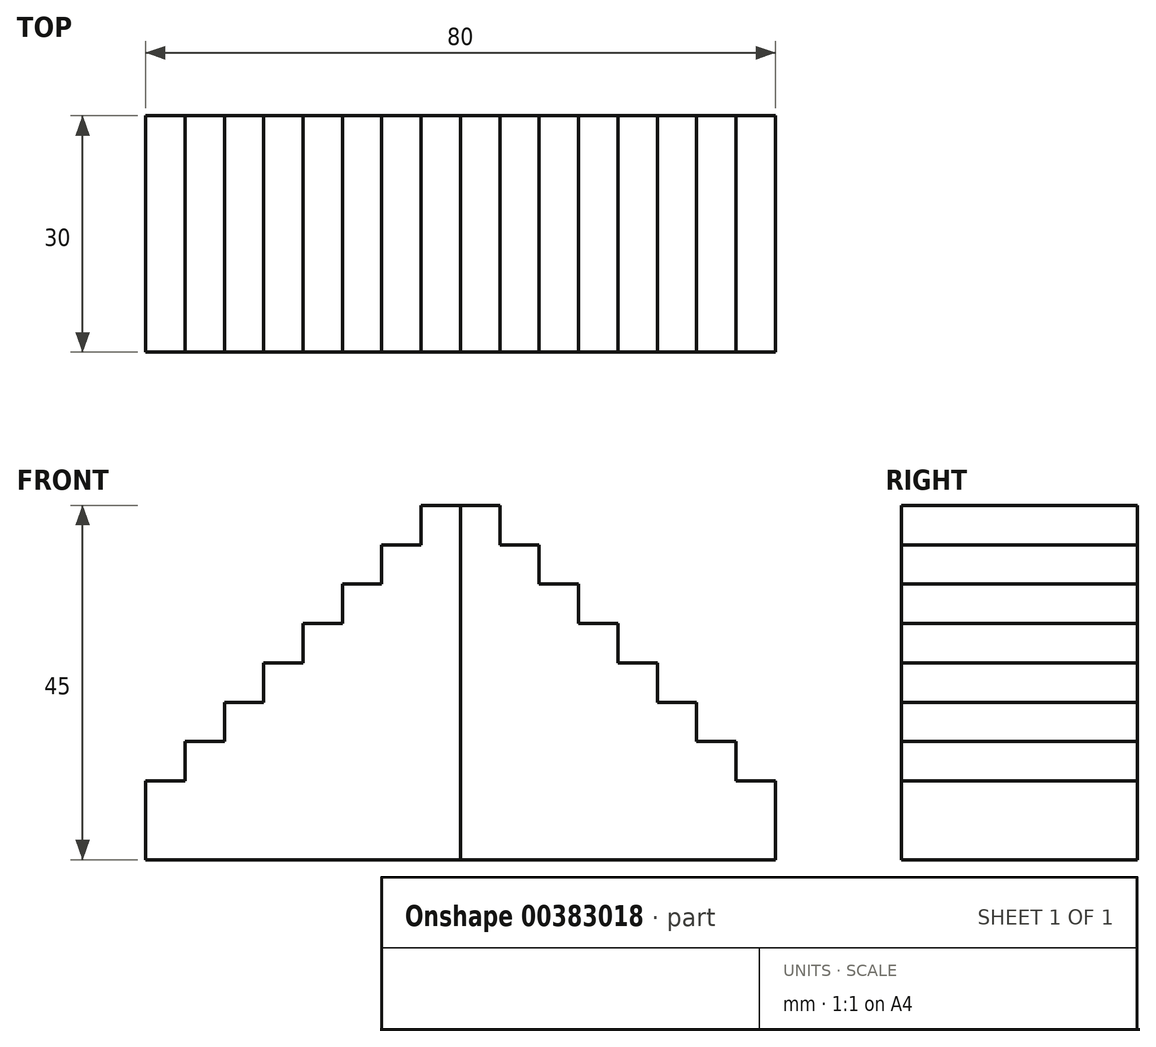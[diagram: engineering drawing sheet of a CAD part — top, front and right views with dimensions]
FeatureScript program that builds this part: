
annotation { "Feature Type Name" : "Feature", "Feature Type Description" : "" }
export const myFeature = defineFeature(function(context is Context, id is Id, definition is map)
    precondition{}
    {
        {
            var Q0;
            Q0=qCreatedBy(makeId("Front.planeOp"),FACE);
            var sketch = newSketch(context, id + "F0", { "sketchPlane" : qUnion([Q0])});
            skLineSegment(sketch, "E0", {"start": v(0, 0) * mm, "end": v(40, 0) * mm});
            skLineSegment(sketch, "E1", {"start": v(40, 0) * mm, "end": v(40, 10) * mm});
            skLineSegment(sketch, "E2", {"start": v(40, 10) * mm, "end": v(35, 10) * mm});
            skLineSegment(sketch, "E3", {"start": v(35, 10) * mm, "end": v(35, 15) * mm});
            skLineSegment(sketch, "E4", {"start": v(35, 15) * mm, "end": v(30, 15) * mm});
            skLineSegment(sketch, "E5", {"start": v(30, 15) * mm, "end": v(30, 20) * mm});
            skLineSegment(sketch, "E6", {"start": v(30, 20) * mm, "end": v(25, 20) * mm});
            skLineSegment(sketch, "E7", {"start": v(25, 20) * mm, "end": v(25, 25) * mm});
            skLineSegment(sketch, "E8", {"start": v(25, 25) * mm, "end": v(20, 25) * mm});
            skLineSegment(sketch, "E9", {"start": v(20, 25) * mm, "end": v(20, 30) * mm});
            skLineSegment(sketch, "E10", {"start": v(20, 30) * mm, "end": v(15, 30) * mm});
            skLineSegment(sketch, "E11", {"start": v(15, 30) * mm, "end": v(15, 35) * mm});
            skLineSegment(sketch, "E12", {"start": v(10, 40) * mm, "end": v(5, 40) * mm});
            skLineSegment(sketch, "E13", {"start": v(5, 40) * mm, "end": v(5, 45) * mm});
            skLineSegment(sketch, "E14", {"start": v(5, 45) * mm, "end": v(0, 45) * mm});
            skLineSegment(sketch, "E15", {"start": v(0, 45) * mm, "end": v(0, 0) * mm});
            skPoint(sketch, "E16.orphan", {"position": v(0, 35) * mm});
            skLineSegment(sketch, "E17", {"start": v(15, 35) * mm, "end": v(10, 35) * mm});
            skLineSegment(sketch, "E18", {"start": v(10, 35) * mm, "end": v(10, 40) * mm});
            skSolve(sketch);
        }
        {
            var Q0;
            Q0 = qSketchRegion(id + "F0", true);
            extrude(context, id + "F1", {"entities" : qUnion([Q0]), "depth" : 30 * mm, "offsetDistance" : 25 * mm});
        }
        {
            var Q0;
            Q0=makeQuery(id+"F1.opExtrude","SWEPT_BODY",BODY,{"disambiguationData":[OSD([sQuery(id+"F0.wireOp",EDGE,"E0"),sQuery(id+"F0.wireOp",EDGE,"E1"),sQuery(id+"F0.wireOp",EDGE,"E2"),sQuery(id+"F0.wireOp",EDGE,"E3"),sQuery(id+"F0.wireOp",EDGE,"E4"),sQuery(id+"F0.wireOp",EDGE,"E5"),sQuery(id+"F0.wireOp",EDGE,"E6"),sQuery(id+"F0.wireOp",EDGE,"E7"),sQuery(id+"F0.wireOp",EDGE,"E8"),sQuery(id+"F0.wireOp",EDGE,"E9"),sQuery(id+"F0.wireOp",EDGE,"E10"),sQuery(id+"F0.wireOp",EDGE,"E11"),sQuery(id+"F0.wireOp",EDGE,"E12"),sQuery(id+"F0.wireOp",EDGE,"E13"),sQuery(id+"F0.wireOp",EDGE,"E14"),sQuery(id+"F0.wireOp",EDGE,"E15"),sQuery(id+"F0.wireOp",EDGE,"E17"),sQuery(id+"F0.wireOp",EDGE,"E18")])]});
            var Q1;
            Q1=qCreatedBy(makeId("Right.planeOp"),FACE);
            mirror(context, id + "F2", {"entities" : qUnion([Q0]), "mirrorPlane" : qUnion([Q1])});
        }
    });
